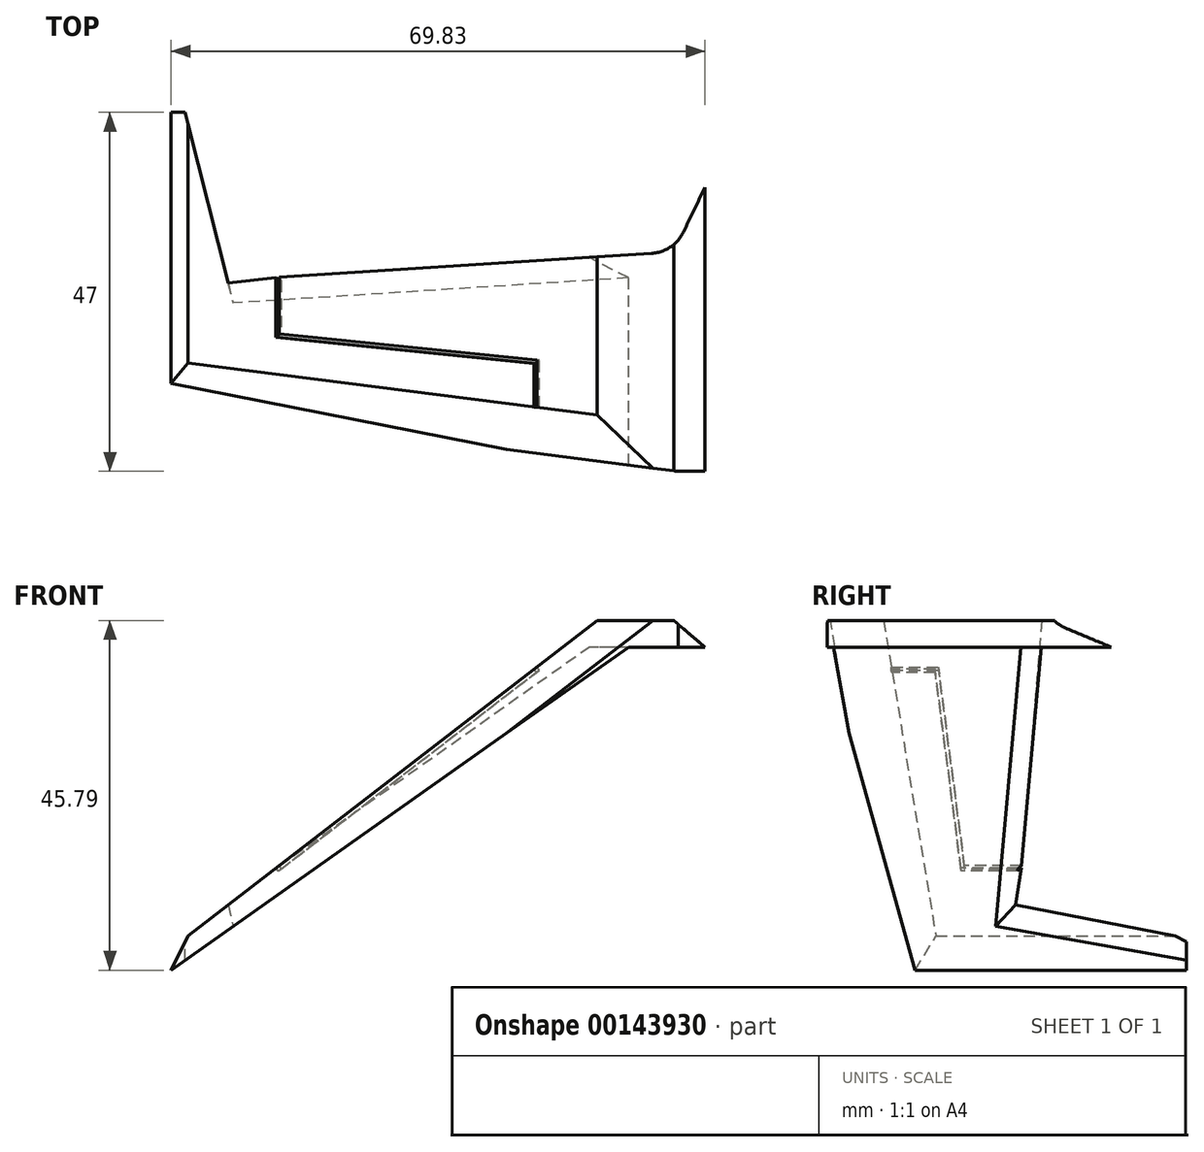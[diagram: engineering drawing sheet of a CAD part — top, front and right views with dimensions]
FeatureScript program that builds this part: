
annotation { "Feature Type Name" : "Feature", "Feature Type Description" : "" }
export const myFeature = defineFeature(function(context is Context, id is Id, definition is map)
    precondition{}
    {
        {
            var Q0;
            Q0=qCreatedBy(makeId("Front.planeOp"),FACE);
            var sketch = newSketch(context, id + "F0", { "sketchPlane" : qUnion([Q0])});
            skLineSegment(sketch, "E0.0", {"start": v(0, 2.5) * mm, "end": v(5.22, 2.5) * mm});
            skFitSpline(sketch, "E1.0", {"points": [v(6.36, 3.47) * mm, v(4.58, 1.94) * mm, v(2.8, 0.41) * mm, v(1, -1.12) * mm]});
            skLineSegment(sketch, "E2", {"start": v(0, 0) * mm, "end": v(0, 2.5) * mm});
            skLineSegment(sketch, "E3", {"start": v(1.73, -0.5) * mm, "end": v(11.73, -0.5) * mm});
            skLineSegment(sketch, "E4", {"start": v(71.73, -40.14) * mm, "end": v(71.73, -42.91) * mm});
            skLineSegment(sketch, "E5", {"start": v(11.73, -0.5) * mm, "end": v(71.73, -42.91) * mm});
            skLineSegment(sketch, "E6", {"start": v(5.8, 3) * mm, "end": v(15.8, 3) * mm});
            skLineSegment(sketch, "E7", {"start": v(0, 0) * mm, "end": v(2.31, 0) * mm});
            skFitSpline(sketch, "E8.trimOffspring", {"points": [v(6.36, 3.47) * mm, v(4.58, 1.94) * mm, v(2.8, 0.41) * mm, v(1, -1.12) * mm]});
            skLineSegment(sketch, "E9", {"start": v(15.8, 3) * mm, "end": v(71.73, -40.14) * mm});
            skSolve(sketch);
        }
        {
            var Q0;
            Q0=qSketchRegion(id+"F0",true);
            extrude(context, id + "F1", {"entities" : qUnion([Q0]), "depth" : 45 * mm});
        }
        {
            var Q0;
            Q0=makeQuery(id+"F1.opExtrude","CAP_FACE",FACE,{"disambiguationData":[OSD([sQuery(id+"F0.wireOp",EDGE,"E0.0"),sQuery(id+"F0.wireOp",EDGE,"E1.0"),sQuery(id+"F0.wireOp",EDGE,"E2"),sQuery(id+"F0.wireOp",EDGE,"E3"),sQuery(id+"F0.wireOp",EDGE,"E4"),sQuery(id+"F0.wireOp",EDGE,"E5"),sQuery(id+"F0.wireOp",EDGE,"E6"),sQuery(id+"F0.wireOp",EDGE,"E7"),sQuery(id+"F0.wireOp",EDGE,"E8.trimOffspring"),sQuery(id+"F0.wireOp",EDGE,"E9")])],"isStart":false});
            var sketch = newSketch(context, id + "F2", { "sketchPlane" : qUnion([Q0])});
            skLineSegment(sketch, "E10", {"start": v(2.31, 0) * mm, "end": v(5.22, 2.5) * mm});
            skLineSegment(sketch, "E11", {"start": v(5.22, 2.5) * mm, "end": v(0, 2.5) * mm});
            skLineSegment(sketch, "E12", {"start": v(0, 2.5) * mm, "end": v(0, 0) * mm});
            skLineSegment(sketch, "E13", {"start": v(0, 0) * mm, "end": v(2.31, 0) * mm});
            skSolve(sketch);
        }
        {
            var Q0;
            Q0=qSketchRegion(id+"F2",true);
            extrude(context, id + "F3", {"entities" : qUnion([Q0]), "operationType" : NewBodyOperationType.REMOVE, "oppositeDirection" : true, "depth" : 5 * mm});
        }
        {
            var Q0;
            Q0=makeQuery(id+"F1.opExtrude","CAP_FACE",FACE,{"disambiguationData":[OSD([sQuery(id+"F0.wireOp",EDGE,"E0.0"),sQuery(id+"F0.wireOp",EDGE,"E1.0"),sQuery(id+"F0.wireOp",EDGE,"E2"),sQuery(id+"F0.wireOp",EDGE,"E3"),sQuery(id+"F0.wireOp",EDGE,"E4"),sQuery(id+"F0.wireOp",EDGE,"E5"),sQuery(id+"F0.wireOp",EDGE,"E6"),sQuery(id+"F0.wireOp",EDGE,"E7"),sQuery(id+"F0.wireOp",EDGE,"E8.trimOffspring"),sQuery(id+"F0.wireOp",EDGE,"E9")])],"isStart":true});
            var sketch = newSketch(context, id + "F4", { "sketchPlane" : qUnion([Q0])});
            skLineSegment(sketch, "E14", {"start": v(-5.22, 2.5) * mm, "end": v(0, 2.5) * mm});
            skLineSegment(sketch, "E15", {"start": v(0, 2.5) * mm, "end": v(0, 0) * mm});
            skLineSegment(sketch, "E16", {"start": v(0, 0) * mm, "end": v(-2.31, 0) * mm});
            skLineSegment(sketch, "E17", {"start": v(-2.31, 0) * mm, "end": v(-5.22, 2.5) * mm});
            skSolve(sketch);
        }
        {
            var Q0;
            Q0=qSketchRegion(id+"F4",true);
            extrude(context, id + "F5", {"entities" : qUnion([Q0]), "operationType" : NewBodyOperationType.REMOVE, "oppositeDirection" : true, "depth" : 15.25 * mm});
        }
        {
            var Q0;
            Q0=makeQuery(id+"F1.opExtrude","CAP_FACE",FACE,{"disambiguationData":[OSD([sQuery(id+"F0.wireOp",EDGE,"E0.0"),sQuery(id+"F0.wireOp",EDGE,"E1.0"),sQuery(id+"F0.wireOp",EDGE,"E2"),sQuery(id+"F0.wireOp",EDGE,"E3"),sQuery(id+"F0.wireOp",EDGE,"E4"),sQuery(id+"F0.wireOp",EDGE,"E5"),sQuery(id+"F0.wireOp",EDGE,"E6"),sQuery(id+"F0.wireOp",EDGE,"E7"),sQuery(id+"F0.wireOp",EDGE,"E8.trimOffspring"),sQuery(id+"F0.wireOp",EDGE,"E9")])],"isStart":false});
            extrude(context, id + "F6", {"entities" : qUnion([Q0]), "operationType" : NewBodyOperationType.REMOVE, "oppositeDirection" : true, "depth" : 2 * mm});
        }
        {
            var Q0;
            Q0=makeQuery(id+"F1.opExtrude","CAP_FACE",FACE,{"disambiguationData":[OSD([sQuery(id+"F0.wireOp",EDGE,"E0.0"),sQuery(id+"F0.wireOp",EDGE,"E1.0"),sQuery(id+"F0.wireOp",EDGE,"E2"),sQuery(id+"F0.wireOp",EDGE,"E3"),sQuery(id+"F0.wireOp",EDGE,"E4"),sQuery(id+"F0.wireOp",EDGE,"E5"),sQuery(id+"F0.wireOp",EDGE,"E6"),sQuery(id+"F0.wireOp",EDGE,"E7"),sQuery(id+"F0.wireOp",EDGE,"E8.trimOffspring"),sQuery(id+"F0.wireOp",EDGE,"E9")])],"isStart":true});
            extrude(context, id + "F7", {"entities" : qUnion([Q0]), "operationType" : NewBodyOperationType.ADD, "depth" : 5 * mm});
        }
        {
            var Q0;
            Q0=makeQuery(id+"F1.opExtrude","SWEPT_FACE",FACE,{"disambiguationData":[OSD([sQuery(id+"F0.wireOp",EDGE,"E6")])]});
            var sketch = newSketch(context, id + "F8", { "sketchPlane" : qUnion([Q0])});
            skLineSegment(sketch, "E18", {"start": v(8.72, -13.47) * mm, "end": v(64.2, -17.01) * mm});
            skLineSegment(sketch, "E19", {"start": v(0, -1.23) * mm, "end": v(0, 6.57) * mm});
            skLineSegment(sketch, "E20", {"start": v(0, 6.57) * mm, "end": v(68.16, 6.57) * mm});
            skLineSegment(sketch, "E21", {"start": v(69.73, 5) * mm, "end": v(64.2, -17.01) * mm});
            skLineSegment(sketch, "E22", {"start": v(68.16, 6.57) * mm, "end": v(69.73, 5) * mm});
            skLineSegment(sketch, "E23.0", {"start": v(0, -42) * mm, "end": v(5.22, -42) * mm});
            skLineSegment(sketch, "E24", {"start": v(5.22, -42) * mm, "end": v(73.13, -33.34) * mm});
            skLineSegment(sketch, "E25", {"start": v(73.13, -33.34) * mm, "end": v(73.13, -45.66) * mm});
            skLineSegment(sketch, "E26", {"start": v(73.13, -45.66) * mm, "end": v(0, -45.66) * mm});
            skLineSegment(sketch, "E27", {"start": v(0, -45.66) * mm, "end": v(0, -42) * mm});
            skLineSegment(sketch, "E28", {"start": v(0, -1.23) * mm, "end": v(4.54, -10.65) * mm});
            skPoint(sketch, "E29.visualSharp", {"position": v(5.8, -13.29) * mm});
            skArc(sketch, "E29.filletArc", {"start": v(4.54, -10.65) * mm, "mid": v(6.25, -12.63) * mm, "end": v(8.72, -13.47) * mm});
            skSolve(sketch);
        }
        {
            var Q0;
            Q0=qSketchRegion(id+"F8",true);
            extrude(context, id + "F9", {"entities" : qUnion([Q0]), "operationType" : NewBodyOperationType.REMOVE, "oppositeDirection" : true, "depth" : 50 * mm});
        }
        {
            var Q0;
            {var subQ0=sQuery(id+"F0.wireOp",EDGE,"E9");Q0=makeQuery(id+"F9.boolean.opBoolean","INTERSECT",EDGE,{"derivedFrom":[makeQuery(id+"F7.boolean.opBoolean","MERGE",FACE,{"derivedFrom":[makeQuery(id+"F1.opExtrude","SWEPT_FACE",FACE,{"disambiguationData":[OSD([subQ0])]}),makeQuery(id+"F7.opExtrude","SWEPT_FACE",FACE,{"disambiguationData":[OSD([subQ0])]})]}),makeQuery(id+"F9.opExtrude","SWEPT_FACE",FACE,{"disambiguationData":[OSD([sQuery(id+"F8.wireOp",EDGE,"E24")])]})]});}
            chamfer(context, id + "F10", {"entities" : qUnion([Q0]), "chamferType" : ChamferType.OFFSET_ANGLE, "width" : 6 * mm, "oppositeDirection" : false, "angle" : 35 * degree});
        }
        {
            var Q0;
            {var subQ0=sQuery(id+"F0.wireOp",EDGE,"E9");var subQ1=sQuery(id+"F0.wireOp",EDGE,"E4");Q0=makeQuery(id+"F7.boolean.opBoolean","MERGE",EDGE,{"derivedFrom":[makeQuery(id+"F1.opExtrude","SWEPT_EDGE",EDGE,{"disambiguationData":[OSD([subQ1,subQ0])]}),makeQuery(id+"F7.opExtrude","SWEPT_EDGE",EDGE,{"disambiguationData":[OSD([subQ1,subQ0])]})]});}
            chamfer(context, id + "F11", {"entities" : qUnion([Q0]), "width" : 3 * mm, "tangentPropagation" : true});
        }
        {
            var Q0;
            {var subQ0=sQuery(id+"F0.wireOp",EDGE,"E5");Q0=makeQuery(id+"F9.boolean.opBoolean","INTERSECT",EDGE,{"derivedFrom":[makeQuery(id+"F7.boolean.opBoolean","MERGE",FACE,{"derivedFrom":[makeQuery(id+"F1.opExtrude","SWEPT_FACE",FACE,{"disambiguationData":[OSD([subQ0])]}),makeQuery(id+"F7.opExtrude","SWEPT_FACE",FACE,{"disambiguationData":[OSD([subQ0])]})]}),makeQuery(id+"F9.opExtrude","SWEPT_FACE",FACE,{"disambiguationData":[OSD([sQuery(id+"F8.wireOp",EDGE,"E18")])]})]});}
            chamfer(context, id + "F12", {"entities" : qUnion([Q0]), "width" : 3 * mm, "tangentPropagation" : true});
        }
        {
            var Q0;
            {var subQ0=sQuery(id+"F0.wireOp",EDGE,"E9");Q0=makeQuery(id+"F7.boolean.opBoolean","MERGE",FACE,{"derivedFrom":[makeQuery(id+"F1.opExtrude","SWEPT_FACE",FACE,{"disambiguationData":[OSD([subQ0])]}),makeQuery(id+"F7.opExtrude","SWEPT_FACE",FACE,{"disambiguationData":[OSD([subQ0])]})]});}
            var sketch = newSketch(context, id + "F13", { "sketchPlane" : qUnion([Q0])});
            skLineSegment(sketch, "E30", {"start": v(63.77, -16.6) * mm, "end": v(63.77, -24.47) * mm});
            skLineSegment(sketch, "E31", {"start": v(63.77, -24.47) * mm, "end": v(21.16, -27.87) * mm});
            skLineSegment(sketch, "E32", {"start": v(21.16, -27.87) * mm, "end": v(21.16, -33.56) * mm});
            skLineSegment(sketch, "E33", {"start": v(21.16, -33.56) * mm, "end": v(20.66, -33.61) * mm});
            skLineSegment(sketch, "E34", {"start": v(20.66, -33.61) * mm, "end": v(20.66, -27.41) * mm});
            skLineSegment(sketch, "E35.0", {"start": v(63.27, -24) * mm, "end": v(20.66, -27.41) * mm});
            skLineSegment(sketch, "E36.0", {"start": v(63.27, -16.58) * mm, "end": v(63.27, -24) * mm});
            skLineSegment(sketch, "E37", {"start": v(63.77, -16.6) * mm, "end": v(63.27, -16.58) * mm});
            skSolve(sketch);
        }
        {
            var Q0;
            Q0=qSketchRegion(id+"F13",true);
            extrude(context, id + "F14", {"entities" : qUnion([Q0]), "operationType" : NewBodyOperationType.REMOVE, "oppositeDirection" : true, "depth" : .5 * mm});
        }
        {
            var Q0;
            Q0=makeQuery(id+"F1.opExtrude","SWEPT_BODY",BODY,{"disambiguationData":[OSD([sQuery(id+"F0.wireOp",EDGE,"E0.0"),sQuery(id+"F0.wireOp",EDGE,"E1.0"),sQuery(id+"F0.wireOp",EDGE,"E2"),sQuery(id+"F0.wireOp",EDGE,"E3"),sQuery(id+"F0.wireOp",EDGE,"E4"),sQuery(id+"F0.wireOp",EDGE,"E5"),sQuery(id+"F0.wireOp",EDGE,"E6"),sQuery(id+"F0.wireOp",EDGE,"E7"),sQuery(id+"F0.wireOp",EDGE,"E8.trimOffspring"),sQuery(id+"F0.wireOp",EDGE,"E9")])]});
            var Q1;
            Q1=qCreatedBy(makeId("Right.planeOp"),FACE);
            mirror(context, id + "F15", {"entities" : qUnion([Q0]), "mirrorPlane" : qUnion([Q1])});
        }
        {
            var Q0;
            Q0=makeQuery(id+"F1.opExtrude","SWEPT_BODY",BODY,{"disambiguationData":[OSD([sQuery(id+"F0.wireOp",EDGE,"E0.0"),sQuery(id+"F0.wireOp",EDGE,"E1.0"),sQuery(id+"F0.wireOp",EDGE,"E2"),sQuery(id+"F0.wireOp",EDGE,"E3"),sQuery(id+"F0.wireOp",EDGE,"E4"),sQuery(id+"F0.wireOp",EDGE,"E5"),sQuery(id+"F0.wireOp",EDGE,"E6"),sQuery(id+"F0.wireOp",EDGE,"E7"),sQuery(id+"F0.wireOp",EDGE,"E8.trimOffspring"),sQuery(id+"F0.wireOp",EDGE,"E9")])]});
            deleteBodies(context, id + "F16", {"entities" : qUnion([Q0])});
        }
    });
